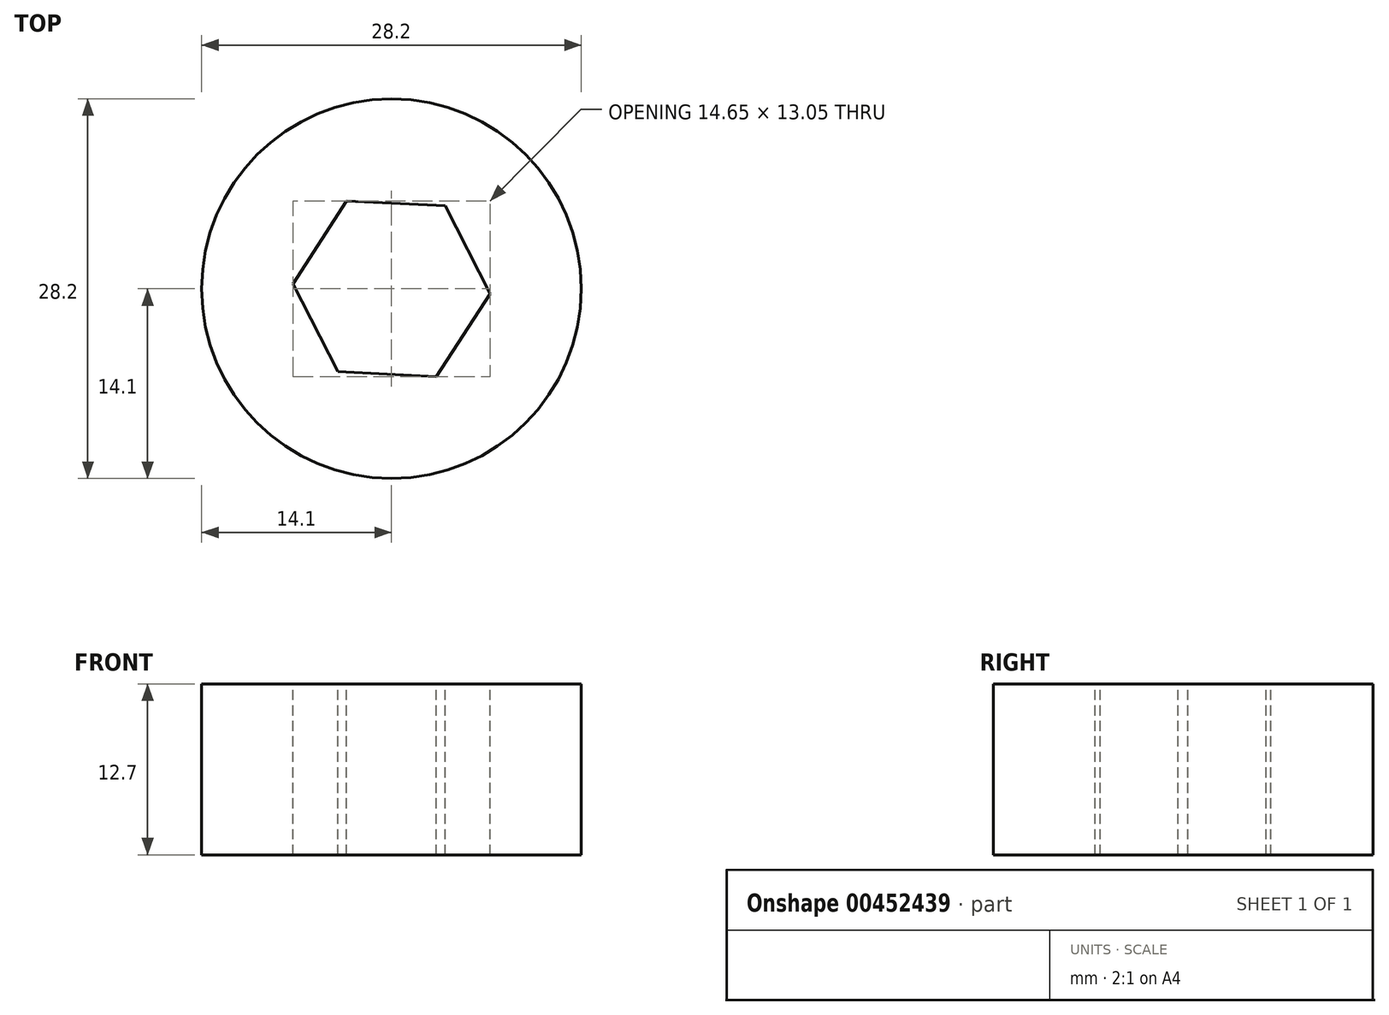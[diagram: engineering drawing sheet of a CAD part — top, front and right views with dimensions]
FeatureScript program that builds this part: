
annotation { "Feature Type Name" : "Feature", "Feature Type Description" : "" }
export const myFeature = defineFeature(function(context is Context, id is Id, definition is map)
    precondition{}
    {
        {
            var Q0;
            Q0=qCreatedBy(makeId("Top.planeOp"),FACE);
            var sketch = newSketch(context, id + "F0", { "sketchPlane" : qUnion([Q0])});
            skCircle(sketch, "E0", {"center": v(0, 0) * mm, "radius": 14.1 * mm});
            skSolve(sketch);
        }
        {
            var Q0;
            Q0=makeQuery(id+"F0.imprint","IMPRINT",FACE,{"disambiguationData":[TD([[makeQuery(id+"F0.imprint","IMPRINT",EDGE,{"derivedFrom":sQuery(id+"F0.wireOp",EDGE,"E0")}),1.0]])]});
            extrude(context, id + "F1", {"entities" : qUnion([Q0]), "depth" : 12.7 * mm});
        }
        {
            var Q0;
            Q0=makeQuery(id+"F1.opExtrude","CAP_FACE",FACE,{"disambiguationData":[OSD([sQuery(id+"F0.wireOp",EDGE,"E0")])],"isStart":false});
            var sketch = newSketch(context, id + "F2", { "sketchPlane" : qUnion([Q0])});
            skCircle(sketch, "E1.cCircle", {"center": v(0, 0) * mm, "radius": 6.35 * mm, "construction": true});
            skLineSegment(sketch, "E1.0", {"start": v(3.98, 6.16) * mm, "end": v(7.32, -0.37) * mm});
            skLineSegment(sketch, "E1.1", {"start": v(7.32, -0.37) * mm, "end": v(3.34, -6.53) * mm});
            skLineSegment(sketch, "E1.2", {"start": v(3.34, -6.53) * mm, "end": v(-3.98, -6.16) * mm});
            skLineSegment(sketch, "E1.3", {"start": v(-3.98, -6.16) * mm, "end": v(-7.32, 0.37) * mm});
            skLineSegment(sketch, "E1.4", {"start": v(-7.32, 0.37) * mm, "end": v(-3.34, 6.53) * mm});
            skLineSegment(sketch, "E1.5", {"start": v(-3.34, 6.53) * mm, "end": v(3.98, 6.16) * mm});
            skPoint(sketch, "E1.0.midPoint", {"position": v(5.65, 2.9) * mm});
            skSolve(sketch);
        }
        {
            var Q0;
            Q0=makeQuery(id+"F2.imprint","IMPRINT",FACE,{"disambiguationData":[TD([[makeQuery(id+"F2.imprint","IMPRINT",EDGE,{"derivedFrom":sQuery(id+"F2.wireOp",EDGE,"E1.0")}),-1.0]])]});
            extrude(context, id + "F3", {"entities" : qUnion([Q0]), "operationType" : NewBodyOperationType.REMOVE, "oppositeDirection" : true, "depth" : 12.7 * mm});
        }
    });
